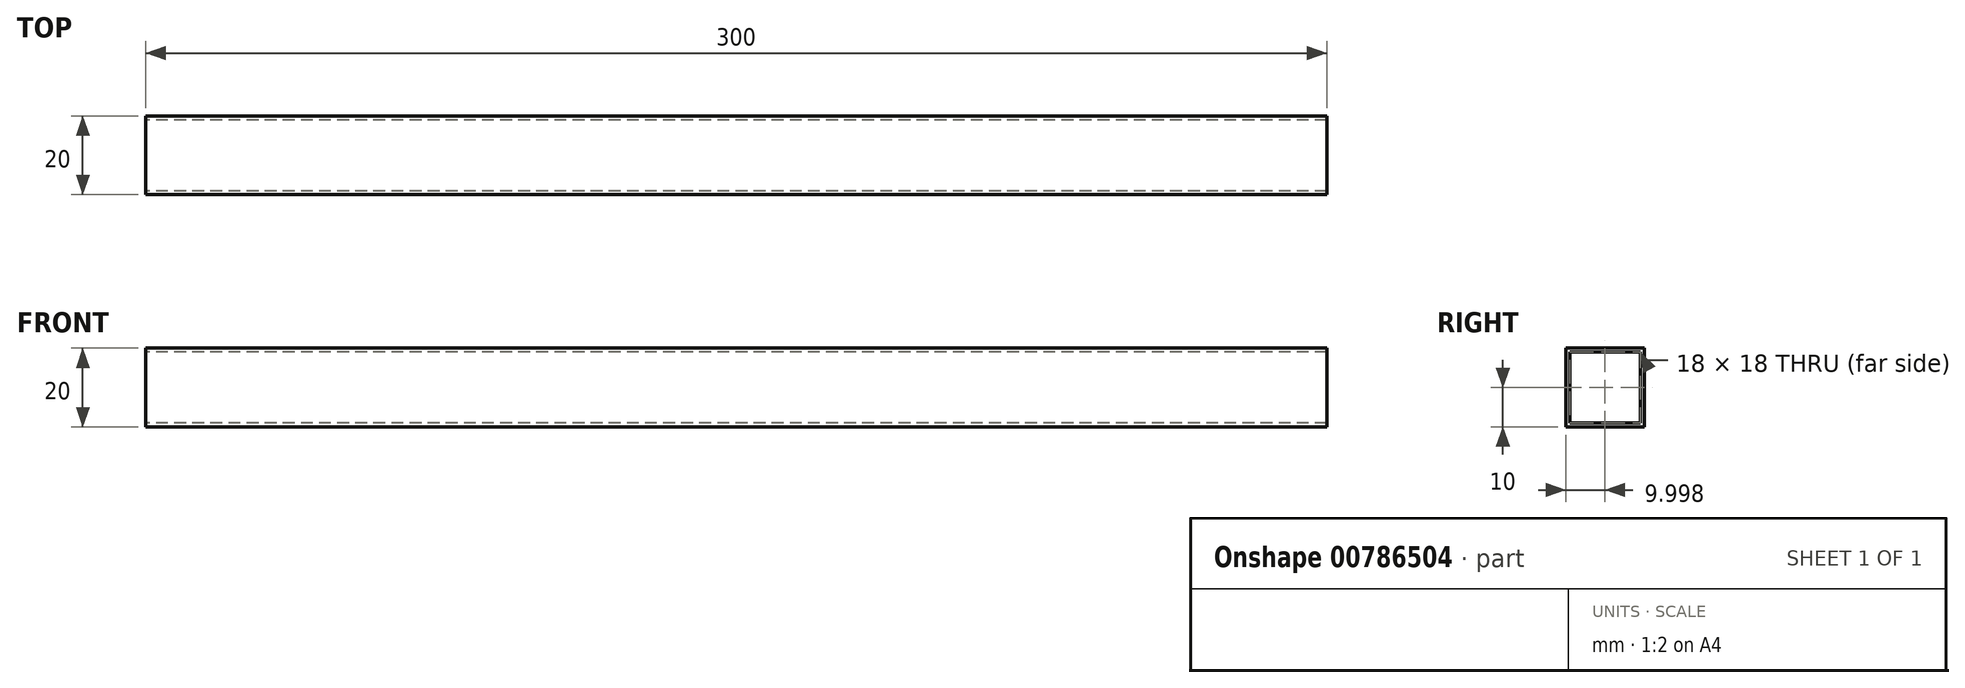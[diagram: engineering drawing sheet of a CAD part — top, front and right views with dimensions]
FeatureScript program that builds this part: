
annotation { "Feature Type Name" : "Feature", "Feature Type Description" : "" }
export const myFeature = defineFeature(function(context is Context, id is Id, definition is map)
    precondition{}
    {
        {
            var Q0;
            Q0=qCreatedBy(makeId("Top.planeOp"),FACE);
            var sketch = newSketch(context, id + "F0", { "sketchPlane" : qUnion([Q0])});
            skLineSegment(sketch, "E0.bottom", {"start": v(24.14, 13.5) * mm, "end": v(324.14, 13.5) * mm});
            skLineSegment(sketch, "E0.top", {"start": v(24.14, -6.5) * mm, "end": v(324.14, -6.5) * mm});
            skLineSegment(sketch, "E0.left", {"start": v(24.14, 13.5) * mm, "end": v(24.14, -6.5) * mm});
            skLineSegment(sketch, "E0.right", {"start": v(324.14, 13.5) * mm, "end": v(324.14, -6.5) * mm});
            skSolve(sketch);
        }
        {
            var Q0;
            Q0 = qSketchRegion(id + "F0", true);
            extrude(context, id + "F1", {"entities" : qUnion([Q0]), "depth" : 20 * mm, "offsetDistance" : 25 * mm});
        }
        {
            var Q0;
            Q0=makeQuery(id+"F1.opExtrude","SWEPT_FACE",FACE,{"disambiguationData":[OSD([sQuery(id+"F0.wireOp",EDGE,"E0.left")])]});
            var sketch = newSketch(context, id + "F2", { "sketchPlane" : qUnion([Q0])});
            skLineSegment(sketch, "E1.bottom", {"start": v(-12.5, 1) * mm, "end": v(5.5, 1) * mm});
            skLineSegment(sketch, "E1.top", {"start": v(-12.5, 19) * mm, "end": v(5.5, 19) * mm});
            skLineSegment(sketch, "E1.left", {"start": v(-12.5, 1) * mm, "end": v(-12.5, 19) * mm});
            skLineSegment(sketch, "E1.right", {"start": v(5.5, 1) * mm, "end": v(5.5, 19) * mm});
            skSolve(sketch);
        }
        {
            var Q0;
            Q0 = qSketchRegion(id + "F2", true);
            extrude(context, id + "F3", {"entities" : qUnion([Q0]), "operationType" : NewBodyOperationType.REMOVE, "oppositeDirection" : true, "depth" : 300 * mm, "offsetDistance" : 25 * mm});
        }
    });
